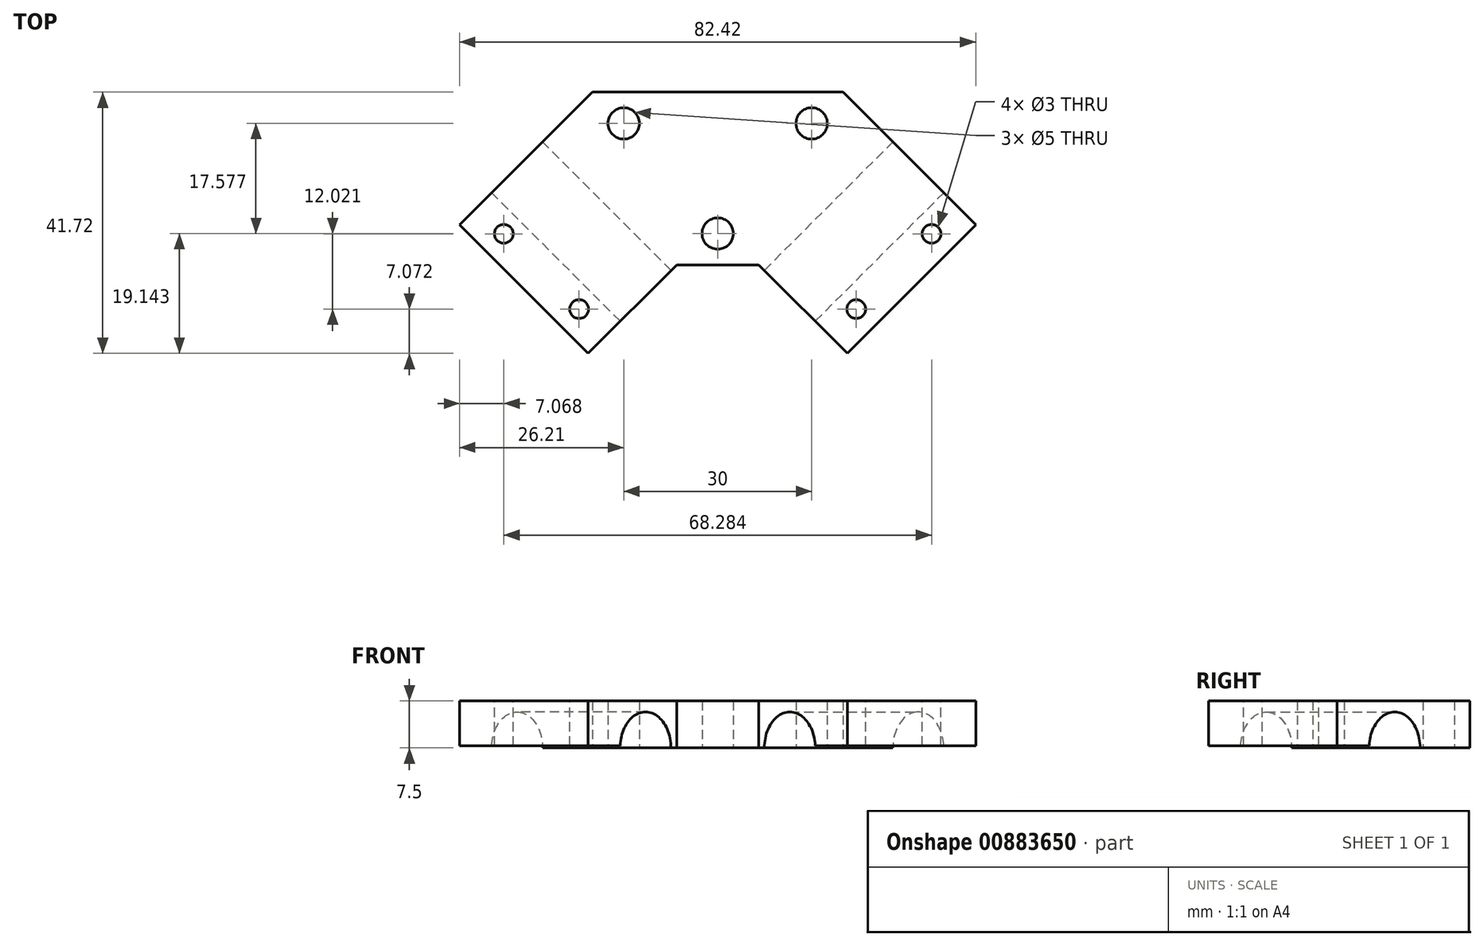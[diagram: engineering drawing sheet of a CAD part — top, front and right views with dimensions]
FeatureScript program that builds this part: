
annotation { "Feature Type Name" : "Feature", "Feature Type Description" : "" }
export const myFeature = defineFeature(function(context is Context, id is Id, definition is map)
    precondition{}
    {
        {
            var Q0;
            Q0=qCreatedBy(makeId("Top.planeOp"),FACE);
            var sketch = newSketch(context, id + "F0", { "sketchPlane" : qUnion([Q0])});
            skLineSegment(sketch, "E0.MirrorCS", {"start": v(-20, 0) * mm, "end": v(-41.21, -21.21) * mm});
            skLineSegment(sketch, "E1.MirrorCS", {"start": v(-41.21, -21.21) * mm, "end": v(-20.7, -41.72) * mm});
            skLineSegment(sketch, "E2.MirrorCS", {"start": v(-20.7, -41.72) * mm, "end": v(-6.56, -27.58) * mm});
            skLineSegment(sketch, "E3.MirrorCS", {"start": v(-6.56, -27.58) * mm, "end": v(0, -27.58) * mm});
            skLineSegment(sketch, "E4.MirrorCS", {"start": v(0, 0) * mm, "end": v(-20, 0) * mm});
            skCircle(sketch, "E5.MirrorC", {"center": v(-15, -5) * mm, "radius": 2.5 * mm});
            skLineSegment(sketch, "E6", {"start": v(0, 0) * mm, "end": v(0, -20.08) * mm});
            skArc(sketch, "E7", {"start": v(0, -20.08) * mm, "mid": v(-2.5, -22.58) * mm, "end": v(0, -25.08) * mm});
            skLineSegment(sketch, "E8.trimOffspring", {"start": v(0, -25.08) * mm, "end": v(0, -27.58) * mm});
            skSolve(sketch);
        }
        {
            var Q0;
            Q0=makeQuery(id+"F0.imprint","IMPRINT",FACE,{"disambiguationData":[TD([[makeQuery(id+"F0.imprint","IMPRINT",EDGE,{"derivedFrom":sQuery(id+"F0.wireOp",EDGE,"E0.MirrorCS")}),1.0]])]});
            extrude(context, id + "F1", {"entities" : qUnion([Q0]), "depth" : 15 * mm, "offsetDistance" : 25 * mm});
        }
        {
            var Q0;
            Q0=makeQuery(id+"F1.opExtrude","SWEPT_FACE",FACE,{"disambiguationData":[OSD([sQuery(id+"F0.wireOp",EDGE,"E0.MirrorCS")])]});
            var sketch = newSketch(context, id + "F2", { "sketchPlane" : qUnion([Q0])});
            skArc(sketch, "E9", {"start": v(36.88, 7.85) * mm, "mid": v(25.4, 7.5) * mm, "end": v(36.88, 7.15) * mm});
            skLineSegment(sketch, "E10", {"start": v(31.14, 7.5) * mm, "end": v(31.14, 15) * mm, "construction": true});
            skLineSegment(sketch, "E11", {"start": v(31.14, 7.5) * mm, "end": v(31.14, 0) * mm, "construction": true});
            skLineSegment(sketch, "E12", {"start": v(31.14, 7.5) * mm, "end": v(44.14, 7.5) * mm, "construction": true});
            skLineSegment(sketch, "E13", {"start": v(44.14, 7.15) * mm, "end": v(36.88, 7.15) * mm});
            skLineSegment(sketch, "E14.MirrorCS", {"start": v(44.14, 7.85) * mm, "end": v(36.88, 7.85) * mm});
            skLineSegment(sketch, "E15", {"start": v(44.14, 7.85) * mm, "end": v(44.14, 7.15) * mm});
            skSolve(sketch);
        }
        {
            var Q0;
            Q0 = qSketchRegion(id + "F2", true);
            extrude(context, id + "F3", {"entities" : qUnion([Q0]), "operationType" : NewBodyOperationType.REMOVE, "endBound" : BoundingType.UP_TO_NEXT, "oppositeDirection" : true, "depth" : 25 * mm, "offsetDistance" : 25 * mm});
        }
        {
            var Q0;
            Q0=makeQuery(id+"F1.opExtrude","CAP_FACE",FACE,{"disambiguationData":[OSD([sQuery(id+"F0.wireOp",EDGE,"E0.MirrorCS"),sQuery(id+"F0.wireOp",EDGE,"E1.MirrorCS"),sQuery(id+"F0.wireOp",EDGE,"E2.MirrorCS"),sQuery(id+"F0.wireOp",EDGE,"E3.MirrorCS"),sQuery(id+"F0.wireOp",EDGE,"E4.MirrorCS"),sQuery(id+"F0.wireOp",EDGE,"E5.MirrorC"),sQuery(id+"F0.wireOp",EDGE,"E6"),sQuery(id+"F0.wireOp",EDGE,"E7"),sQuery(id+"F0.wireOp",EDGE,"E8.trimOffspring")])],"isStart":false});
            var sketch = newSketch(context, id + "F4", { "sketchPlane" : qUnion([Q0])});
            skLineSegment(sketch, "E16", {"start": v(-36.97, -25.46) * mm, "end": v(-34.14, -22.63) * mm, "construction": true});
            skLineSegment(sketch, "E17", {"start": v(-30.96, -31.47) * mm, "end": v(-22.54, -23.05) * mm, "construction": true});
            skLineSegment(sketch, "E18", {"start": v(-34.14, -22.63) * mm, "end": v(-38.38, -18.38) * mm, "construction": true});
            skCircle(sketch, "E19", {"center": v(-34.14, -22.63) * mm, "radius": 1.5 * mm});
            skCircle(sketch, "E20.MirrorC", {"center": v(-22.12, -34.65) * mm, "radius": 1.5 * mm});
            skSolve(sketch);
        }
        {
            var Q0;
            Q0 = qSketchRegion(id + "F4", true);
            extrude(context, id + "F5", {"entities" : qUnion([Q0]), "operationType" : NewBodyOperationType.REMOVE, "endBound" : BoundingType.UP_TO_NEXT, "oppositeDirection" : true, "depth" : 25 * mm, "offsetDistance" : 25 * mm});
        }
        {
            var Q0;
            {var subQ0=makeQuery(id+"F1.opExtrude","CAP_FACE",FACE,{"disambiguationData":[OSD([sQuery(id+"F0.wireOp",EDGE,"E0.MirrorCS"),sQuery(id+"F0.wireOp",EDGE,"E1.MirrorCS"),sQuery(id+"F0.wireOp",EDGE,"E2.MirrorCS"),sQuery(id+"F0.wireOp",EDGE,"E3.MirrorCS"),sQuery(id+"F0.wireOp",EDGE,"E4.MirrorCS"),sQuery(id+"F0.wireOp",EDGE,"E5.MirrorC"),sQuery(id+"F0.wireOp",EDGE,"E6"),sQuery(id+"F0.wireOp",EDGE,"E7"),sQuery(id+"F0.wireOp",EDGE,"E8.trimOffspring")])],"isStart":true});Q0=makeQuery(id+"F8.boolean.opBoolean","MERGE",FACE,{"derivedFrom":[subQ0,makeQuery(id+"F8.opPattern","COPY",FACE,{"derivedFrom":subQ0,"instanceName":"1"})]});}
            var sketch = newSketch(context, id + "F6", { "sketchPlane" : qUnion([Q0])});
            skCircle(sketch, "E21.0", {"center": v(-34.14, 22.63) * mm, "radius": 1.25 * mm, "construction": true});
            skCircle(sketch, "E22.0", {"center": v(-22.12, 34.65) * mm, "radius": 1.25 * mm, "construction": true});
            skCircle(sketch, "E23", {"center": v(-22.12, 34.65) * mm, "radius": 1 * mm});
            skCircle(sketch, "E24", {"center": v(-34.14, 22.63) * mm, "radius": 1 * mm});
            skSolve(sketch);
        }
        {
            var Q0;
            Q0 = qSketchRegion(id + "F6", true);
            extrude(context, id + "F7", {"entities" : qUnion([Q0]), "operationType" : NewBodyOperationType.REMOVE, "endBound" : BoundingType.UP_TO_NEXT, "oppositeDirection" : true, "depth" : 25 * mm, "offsetDistance" : 25 * mm});
        }
        {
            var Q0;
            Q0=makeQuery(id+"F1.opExtrude","SWEPT_BODY",BODY,{"disambiguationData":[OSD([sQuery(id+"F0.wireOp",EDGE,"E0.MirrorCS"),sQuery(id+"F0.wireOp",EDGE,"E1.MirrorCS"),sQuery(id+"F0.wireOp",EDGE,"E2.MirrorCS"),sQuery(id+"F0.wireOp",EDGE,"E3.MirrorCS"),sQuery(id+"F0.wireOp",EDGE,"E4.MirrorCS"),sQuery(id+"F0.wireOp",EDGE,"E5.MirrorC"),sQuery(id+"F0.wireOp",EDGE,"E6")])]});
            var Q1;
            Q1=qCreatedBy(makeId("Right.planeOp"),FACE);
            mirror(context, id + "F8", {"operationType" : NewBodyOperationType.ADD, "entities" : qUnion([Q0]), "mirrorPlane" : qUnion([Q1])});
        }
        {
            var Q0;
            {var subQ0=makeQuery(id+"F1.opExtrude","SWEPT_FACE",FACE,{"disambiguationData":[OSD([sQuery(id+"F0.wireOp",EDGE,"E4.MirrorCS")])]});Q0=makeQuery(id+"F8.boolean.opBoolean","MERGE",FACE,{"derivedFrom":[subQ0,makeQuery(id+"F8.opPattern","COPY",FACE,{"derivedFrom":subQ0,"instanceName":"1"})]});}
            var sketch = newSketch(context, id + "F9", { "sketchPlane" : qUnion([Q0])});
            skLineSegment(sketch, "E25.bottom", {"start": v(-20, 7.5) * mm, "end": v(47.51, 7.5) * mm});
            skLineSegment(sketch, "E26.top", {"start": v(-20, 7.5) * mm, "end": v(-48.87, 7.5) * mm});
            skLineSegment(sketch, "E27.bottom", {"start": v(-48.87, 7.5) * mm, "end": v(47.46, 7.5) * mm});
            skLineSegment(sketch, "E27.top", {"start": v(-48.87, -7.04) * mm, "end": v(47.46, -7.04) * mm});
            skLineSegment(sketch, "E27.left", {"start": v(-48.87, 7.5) * mm, "end": v(-48.87, -7.04) * mm});
            skLineSegment(sketch, "E27.right", {"start": v(47.46, 7.5) * mm, "end": v(47.46, -7.04) * mm});
            skSolve(sketch);
        }
        {
            var Q0;
            Q0 = qSketchRegion(id + "F9", true);
            extrude(context, id + "F10", {"entities" : qUnion([Q0]), "operationType" : NewBodyOperationType.REMOVE, "oppositeDirection" : true, "depth" : 55 * mm, "offsetDistance" : 25 * mm});
        }
    });
